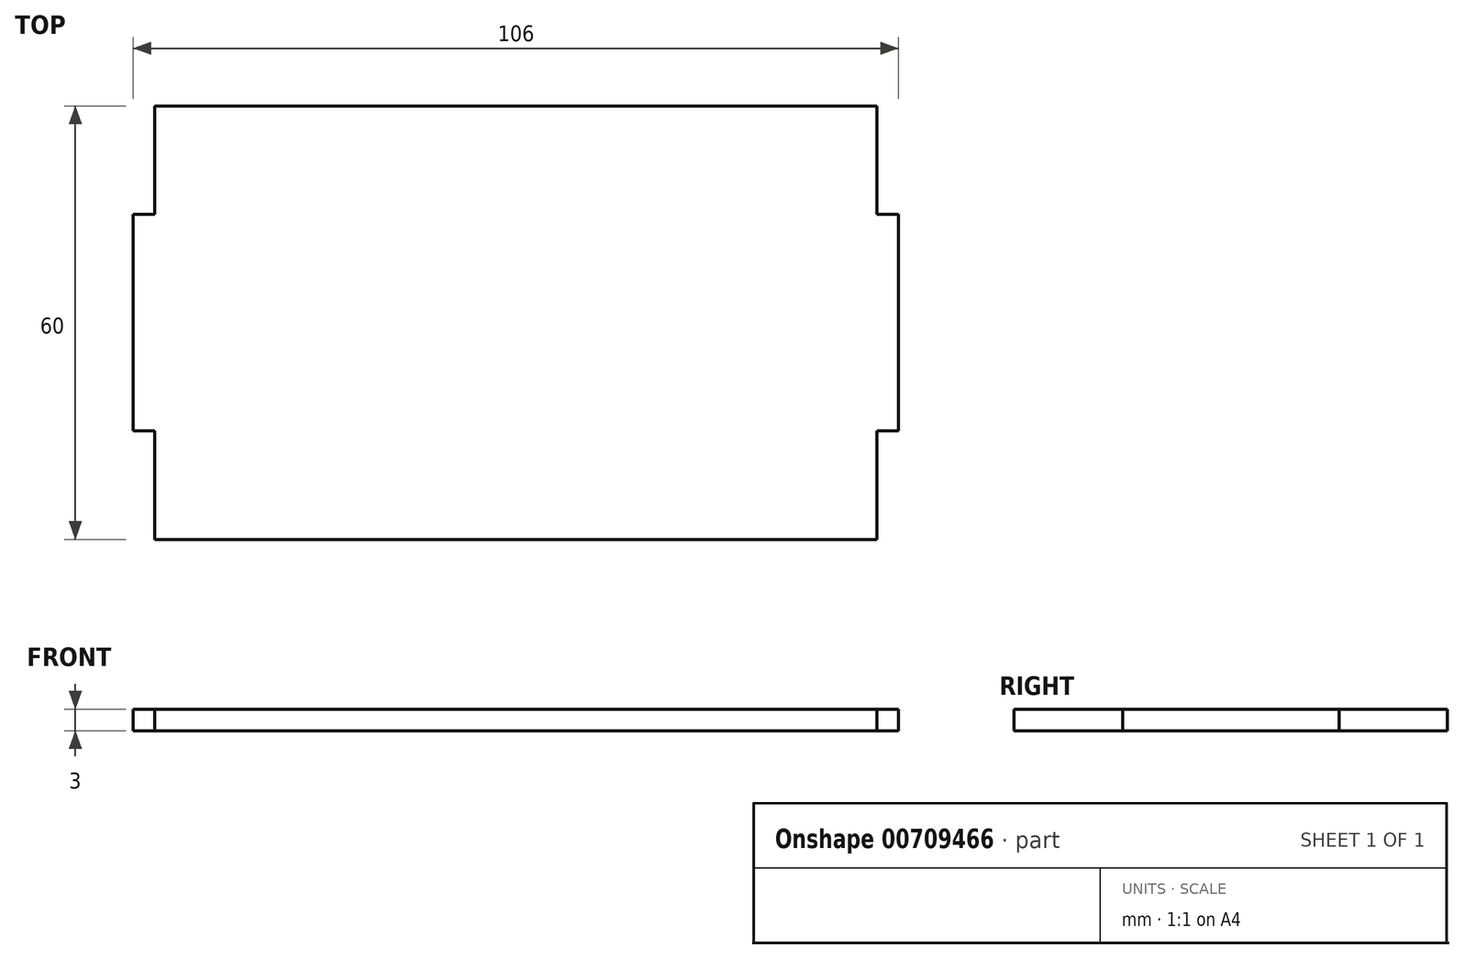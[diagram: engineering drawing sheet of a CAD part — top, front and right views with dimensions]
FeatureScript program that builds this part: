
annotation { "Feature Type Name" : "Feature", "Feature Type Description" : "" }
export const myFeature = defineFeature(function(context is Context, id is Id, definition is map)
    precondition{}
    {
        {
            var Q0;
            Q0=qCreatedBy(makeId("Top.planeOp"),FACE);
            var sketch = newSketch(context, id + "F0", { "sketchPlane" : qUnion([Q0])});
            skLineSegment(sketch, "E0.bottom", {"start": v(-50, 30) * mm, "end": v(50, 30) * mm});
            skLineSegment(sketch, "E0.top", {"start": v(-50, -30) * mm, "end": v(50, -30) * mm});
            skLineSegment(sketch, "E0.left", {"start": v(-50, 30) * mm, "end": v(-50, -30) * mm});
            skLineSegment(sketch, "E0.right", {"start": v(50, 30) * mm, "end": v(50, -30) * mm});
            skPoint(sketch, "E0.middle", {"position": v(0, 0) * mm});
            skLineSegment(sketch, "E1.bottom", {"start": v(-50, 15) * mm, "end": v(-53, 15) * mm});
            skLineSegment(sketch, "E1.top", {"start": v(-50, -15) * mm, "end": v(-53, -15) * mm});
            skLineSegment(sketch, "E1.left", {"start": v(-50, 15) * mm, "end": v(-50, -15) * mm});
            skLineSegment(sketch, "E1.right", {"start": v(-53, 15) * mm, "end": v(-53, -15) * mm});
            skLineSegment(sketch, "E2.MirrorCS", {"start": v(53, 15) * mm, "end": v(53, -15) * mm});
            skLineSegment(sketch, "E3.MirrorCS", {"start": v(50, 15) * mm, "end": v(53, 15) * mm});
            skLineSegment(sketch, "E4.MirrorCS", {"start": v(50, -15) * mm, "end": v(53, -15) * mm});
            skSolve(sketch);
        }
        {
            var Q0;
            Q0=qSketchRegion(id+"F0",true);
            extrude(context, id + "F1", {"entities" : qUnion([Q0]), "depth" : 3 * mm, "offsetDistance" : 25 * mm});
        }
    });
